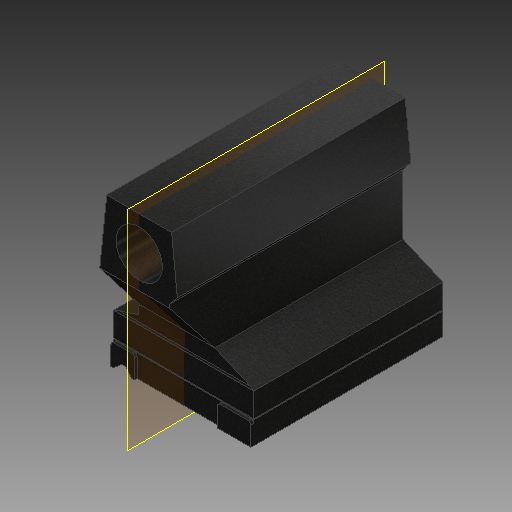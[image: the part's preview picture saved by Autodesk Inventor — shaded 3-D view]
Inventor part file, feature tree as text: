
AUTODESK INVENTOR PART (.ipt)
format: ipt  version: 2018 (Build 220112000, 112)  size: 500,736 bytes
history: native  units: mm
features: extrude x26, sketch x26, fillet x6, plane x2
ambient origin geometry x8: Origin, YZ Plane, XZ Plane, XY Plane, X Axis, Y Axis, Z Axis, Center Point
bodies: Solid1 (feature_tree)
feature tree (60):
  extrude  "Extrusion1"  Depth=151.0mm
  extrude  "Extrusion2"  Depth=203.0mm
  extrude  "Extrusion3"  TaperAngle=135.0deg  [1 undecoded]
  extrude  "Extrusion4"  Depth=10.0mm
  extrude  "Extrusion5"  Depth=28.0mm
  extrude  "Extrusion6"  Depth=2.0mm TaperAngle=0.0deg
  fillet  "Fillet1"  Radius=37.0mm
  extrude  "Extrusion7"  Depth=1.0mm TaperAngle=0.0deg
  fillet  "Fillet3"  Radius=5.0mm
  extrude  "Extrusion8"  Depth=5.0mm
  extrude  "Extrusion9"  Depth=1.0mm
  extrude  "Extrusion10"  Depth=1.0mm
  extrude  "Extrusion11"  Depth=1.0mm TaperAngle=0.0deg
  plane  "Work Plane1"
  extrude  "Extrusion12"  Depth=49.0mm TaperAngle=0.0deg
  extrude  "Extrusion13"  Depth=35.0mm
  extrude  "Extrusion14"  Depth=16.755161mm
  extrude  "Extrusion15"  Depth=295.5mm TaperAngle=0.0deg
  fillet  "Fillet4"  Radius=295.5mm
  extrude  "Extrusion16"  Depth=295.5mm TaperAngle=0.0deg
  extrude  "Extrusion17"  Depth=2.0mm
  plane  "Work Plane2"
  extrude  "Extrusion18"  Depth=50.0mm
  extrude  "Extrusion19"  Depth=5.0mm TaperAngle=0.0deg
  extrude  "Extrusion20"  Depth=1.0mm TaperAngle=0.0deg
  extrude  "Extrusion21"  Depth=207.0mm TaperAngle=0.0deg
  extrude  "Extrusion22"  Depth=204.0mm
  extrude  "Extrusion23"  Depth=6.981317mm
  extrude  "Extrusion24"  Depth=204.0mm TaperAngle=0.0deg
  fillet  "Fillet5"  Radius=25.3mm
  fillet  "Fillet6"  Radius=3.0mm
  extrude  "Extrusion25"  Depth=3.0mm
  fillet  "Fillet7"  Radius=36.2mm
  extrude  "Extrusion26"  Depth=3.0mm
  sketch  "Sketch1"  dims[d19=26.0mm d20=151.0mm]
  sketch  "Sketch2"  dims[d21=203.0mm d22=0.0mm d23=28.0mm]
  sketch  "Sketch3"  dims[d29=4.0mm d30=135.0deg]
  sketch  "Sketch4"  dims[d31=45.0deg d32=10.0mm]
  sketch  "Sketch5"  dims[d33=215.0mm d34=0.0mm d35=28.0mm]
  sketch  "Sketch6"  dims[d36=6.0mm d37=0.0mm d38=2.0mm d39=0.0mm d40=37.0mm]
  sketch  "Sketch8"  dims[d41=6.0mm d42=0.0mm d43=1.0mm d44=0.0mm d45=5.0mm]
  sketch  "Sketch9"  dims[d47=1.0mm d48=0.0mm d49=5.0mm]
  sketch  "Sketch10"  dims[d50=1.0mm d51=1.0mm]
  sketch  "Sketch11"  dims[d52=1.0mm d53=1.0mm]
  sketch  "Sketch12"  dims[d54=1.0mm d55=0.0mm d56=26.0mm d57=0.0mm]
  sketch  "Sketch13"  dims[d58=49.0mm d59=152.0mm d60=0.0mm]
  sketch  "Sketch14"  dims[d61=35.0mm d62=35.0mm]
  sketch  "Sketch15"  dims[d63=16.755161mm d64=16.755161mm]
  sketch  "Sketch16"  dims[d65=58.0mm d66=295.5mm d67=0.0mm d68=295.5mm d69=0.0mm]
  sketch  "Sketch18"  dims[d70=295.5mm d71=0.0mm d72=295.5mm d73=0.0mm]
  sketch  "Sketch19"  dims[d74=1.0mm d75=0.0mm d76=2.0mm]
  sketch  "Sketch20"  dims[d85=1.0mm d86=0.0mm d87=50.0mm]
  sketch  "Sketch21"  dims[d88=300.0mm d89=0.0mm d90=5.0mm d91=0.0mm]
  sketch  "Sketch23"  dims[d92=1.0mm d93=0.0mm d94=1.0mm d95=0.0mm]
  sketch  "Sketch24"  dims[d96=2.0mm d97=207.0mm d98=0.0mm]
  sketch  "Sketch25"  dims[d99=204.0mm d100=0.0mm d101=148.124mm]
  sketch  "Sketch26"  dims[d102=10.2mm d103=6.981317mm]
  sketch  "Sketch27"  dims[d104=3.8mm d106=204.0mm d107=0.0mm d108=25.3mm d109=3.0mm d110=0.0mm]
  sketch  "Sketch28"  dims[d111=3.0mm d112=3.0mm d113=36.2mm]
  sketch  "Sketch29"  dims[d114=3.0mm d115=0.0mm d116=3.0mm d117=2.0mm d118=24.43461mm d121=4.0mm d122=8.0mm d123=22.68928mm d124=10.0mm d125=0.0mm]
note: 1 required parameter value undecoded (feature->parameter linkage not recoverable at this tier; creation-order binding heuristic only, values carry confidence <= 0.55)
